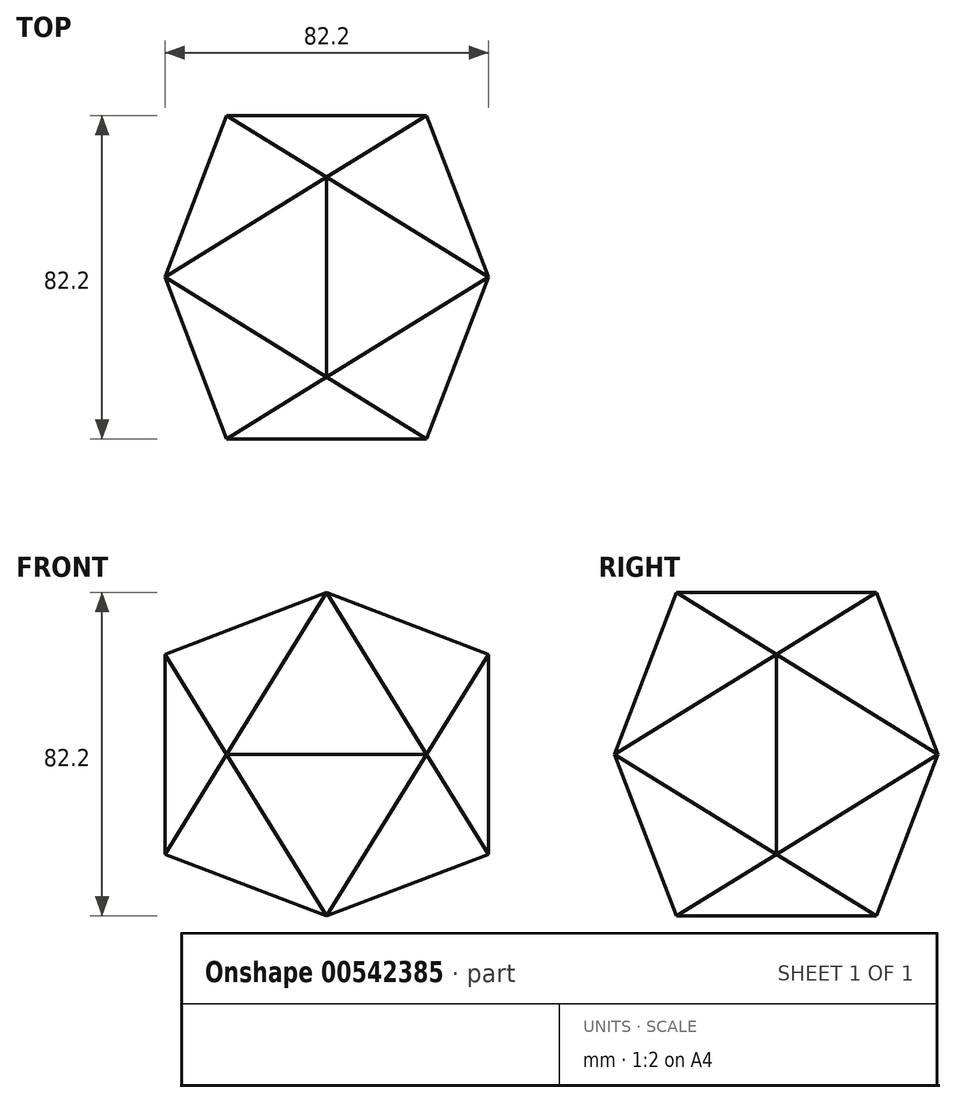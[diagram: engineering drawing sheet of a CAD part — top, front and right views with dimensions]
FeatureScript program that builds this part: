
annotation { "Feature Type Name" : "Feature", "Feature Type Description" : "" }
export const myFeature = defineFeature(function(context is Context, id is Id, definition is map)
    precondition{}
    {
        {
            var Q0;
            Q0=qCreatedBy(makeId("Front.planeOp"),FACE);
            var sketch = newSketch(context, id + "F0", { "sketchPlane" : qUnion([Q0])});
            skLineSegment(sketch, "E0.bottom", {"start": v(41.1, -25.4) * mm, "end": v(-41.1, -25.4) * mm});
            skLineSegment(sketch, "E0.top", {"start": v(41.1, 25.4) * mm, "end": v(-41.1, 25.4) * mm});
            skLineSegment(sketch, "E0.left", {"start": v(41.1, -25.4) * mm, "end": v(41.1, 25.4) * mm});
            skLineSegment(sketch, "E0.right", {"start": v(-41.1, -25.4) * mm, "end": v(-41.1, 25.4) * mm});
            skPoint(sketch, "E0.middle", {"position": v(0, 0) * mm});
            skSolve(sketch);
        }
        {
            var Q0;
            Q0=qCreatedBy(makeId("Front.planeOp"),FACE);
            var sketch = newSketch(context, id + "F1", { "sketchPlane" : qUnion([Q0])});
            skArc(sketch, "E1", {"start": v(0, -48.31) * mm, "mid": v(48.31, 0) * mm, "end": v(0, 48.31) * mm});
            skLineSegment(sketch, "E2", {"start": v(0, -48.31) * mm, "end": v(0, 48.31) * mm});
            skSolve(sketch);
        }
        {
            var Q0;
            Q0=makeQuery(id+"F1.imprint","IMPRINT",FACE,{"disambiguationData":[TD([[makeQuery(id+"F1.imprint","IMPRINT",EDGE,{"derivedFrom":sQuery(id+"F1.wireOp",EDGE,"E1")}),1.0]])]});
            var sketch = newSketch(context, id + "F2", { "sketchPlane" : qUnion([Q0])});
            skLineSegment(sketch, "E3", {"start": v(0, 0) * mm, "end": v(0, 112.6) * mm, "construction": true});
            skSolve(sketch);
        }
        {
            var Q0;
            Q0=makeQuery(id+"F1.imprint","IMPRINT",FACE,{"disambiguationData":[TD([[makeQuery(id+"F1.imprint","IMPRINT",EDGE,{"derivedFrom":sQuery(id+"F1.wireOp",EDGE,"E1")}),1.0]])]});
            var Q1;
            Q1=sQuery(id+"F1.wireOp",EDGE,"E1");
            var Q2;
            Q2=sQuery(id+"F2.wireOp",EDGE,"E3");
            revolve(context, id + "F3", {"entities" : qUnion([Q0]), "surfaceEntities" : qUnion([Q1]), "axis" : qUnion([Q2]), "revolveType" : RevolveType.FULL});
        }
        {
            var Q0;
            Q0=qCreatedBy(makeId("Top.planeOp"),FACE);
            var sketch = newSketch(context, id + "F4", { "sketchPlane" : qUnion([Q0])});
            skLineSegment(sketch, "E4.bottom", {"start": v(25.4, 41.1) * mm, "end": v(-25.4, 41.1) * mm});
            skLineSegment(sketch, "E4.top", {"start": v(25.4, -41.1) * mm, "end": v(-25.4, -41.1) * mm});
            skLineSegment(sketch, "E4.left", {"start": v(25.4, 41.1) * mm, "end": v(25.4, -41.1) * mm});
            skLineSegment(sketch, "E4.right", {"start": v(-25.4, 41.1) * mm, "end": v(-25.4, -41.1) * mm});
            skPoint(sketch, "E4.middle", {"position": v(0, 0) * mm});
            skSolve(sketch);
        }
        {
            var Q0;
            Q0=qCreatedBy(makeId("Right.planeOp"),FACE);
            var sketch = newSketch(context, id + "F5", { "sketchPlane" : qUnion([Q0])});
            skLineSegment(sketch, "E5.bottom", {"start": v(25.4, -41.1) * mm, "end": v(-25.4, -41.1) * mm});
            skLineSegment(sketch, "E5.top", {"start": v(25.4, 41.1) * mm, "end": v(-25.4, 41.1) * mm});
            skLineSegment(sketch, "E5.left", {"start": v(25.4, -41.1) * mm, "end": v(25.4, 41.1) * mm});
            skLineSegment(sketch, "E5.right", {"start": v(-25.4, -41.1) * mm, "end": v(-25.4, 41.1) * mm});
            skPoint(sketch, "E5.middle", {"position": v(0, 0) * mm});
            skSolve(sketch);
        }
        {
            var Q0;
            Q0=sQuery(id+"F5.wireOp",VERTEX,"E5.right.end");
            var Q1;
            Q1=sQuery(id+"F0.wireOp",VERTEX,"E0.left.end");
            var Q2;
            Q2=sQuery(id+"F5.wireOp",VERTEX,"E5.left.end");
            cPlane(context, id + "F6", {"entities" : qUnion([Q0, Q1, Q2]), "cplaneType" : CPlaneType.THREE_POINT, "offset" : 25.4 * mm, "width" : 152.4 * mm, "height" : 152.4 * mm});
        }
        {
            var Q0;
            Q0=qCreatedBy(id+"F6.planeOp",FACE);
            var sketch = newSketch(context, id + "F7", { "sketchPlane" : qUnion([Q0])});
            skCircle(sketch, "E6", {"center": v(0, 0) * mm, "radius": 29.33 * mm});
            skSolve(sketch);
        }
        {
            var Q0;
            Q0 = qSketchRegion(id + "F7", true);
            var Q1;
            Q1=makeQuery(id+"F3.opRevolve","SWEPT_BODY",BODY,{"disambiguationData":[OSD([sQuery(id+"F1.wireOp",EDGE,"E1")])]});
            extrude(context, id + "F8", {"entities" : qUnion([Q0]), "operationType" : NewBodyOperationType.REMOVE, "endBound" : BoundingType.UP_TO_NEXT, "oppositeDirection" : true, "depth" : 25.4 * mm, "endBoundEntityBody" : qUnion([Q1]), "offsetDistance" : 25.4 * mm});
        }
        {
            var Q0;
            Q0=sQuery(id+"F0.wireOp",VERTEX,"E0.right.end");
            var Q1;
            Q1=sQuery(id+"F5.wireOp",VERTEX,"E5.right.end");
            var Q2;
            Q2=sQuery(id+"F5.wireOp",VERTEX,"E5.left.end");
            cPlane(context, id + "F9", {"entities" : qUnion([Q0, Q1, Q2]), "cplaneType" : CPlaneType.THREE_POINT, "offset" : 25.4 * mm, "width" : 152.4 * mm, "height" : 152.4 * mm});
        }
        {
            var Q0;
            Q0=qCreatedBy(id+"F9.planeOp",FACE);
            var sketch = newSketch(context, id + "F10", { "sketchPlane" : qUnion([Q0])});
            skCircle(sketch, "E7", {"center": v(0, 0) * mm, "radius": 29.33 * mm});
            skSolve(sketch);
        }
        {
            var Q0;
            Q0 = qSketchRegion(id + "F10", true);
            extrude(context, id + "F11", {"entities" : qUnion([Q0]), "operationType" : NewBodyOperationType.REMOVE, "endBound" : BoundingType.UP_TO_NEXT, "oppositeDirection" : true, "depth" : 25.4 * mm, "offsetDistance" : 25.4 * mm});
        }
        {
            var Q0;
            Q0=sQuery(id+"F4.wireOp",VERTEX,"E4.right.end");
            var Q1;
            Q1=sQuery(id+"F0.wireOp",VERTEX,"E0.right.end");
            var Q2;
            Q2=sQuery(id+"F5.wireOp",VERTEX,"E5.right.end");
            cPlane(context, id + "F12", {"entities" : qUnion([Q0, Q1, Q2]), "cplaneType" : CPlaneType.THREE_POINT, "offset" : 25.4 * mm, "width" : 152.4 * mm, "height" : 152.4 * mm});
        }
        {
            var Q0;
            Q0=qCreatedBy(id+"F12.planeOp",FACE);
            var sketch = newSketch(context, id + "F13", { "sketchPlane" : qUnion([Q0])});
            skCircle(sketch, "E8", {"center": v(0, 0) * mm, "radius": 29.33 * mm});
            skSolve(sketch);
        }
        {
            var Q0;
            Q0 = qSketchRegion(id + "F13", true);
            extrude(context, id + "F14", {"entities" : qUnion([Q0]), "operationType" : NewBodyOperationType.REMOVE, "endBound" : BoundingType.UP_TO_NEXT, "depth" : 25.4 * mm, "offsetDistance" : 25.4 * mm});
        }
        {
            var Q0;
            Q0=sQuery(id+"F4.wireOp",VERTEX,"E4.right.end");
            var Q1;
            Q1=sQuery(id+"F5.wireOp",VERTEX,"E5.right.end");
            var Q2;
            Q2=sQuery(id+"F4.wireOp",VERTEX,"E4.left.end");
            cPlane(context, id + "F15", {"entities" : qUnion([Q0, Q1, Q2]), "cplaneType" : CPlaneType.THREE_POINT, "offset" : 25.4 * mm, "width" : 152.4 * mm, "height" : 152.4 * mm});
        }
        {
            var Q0;
            Q0=qCreatedBy(id+"F15.planeOp",FACE);
            var sketch = newSketch(context, id + "F16", { "sketchPlane" : qUnion([Q0])});
            skCircle(sketch, "E9", {"center": v(0, 0) * mm, "radius": 29.33 * mm});
            skSolve(sketch);
        }
        {
            var Q0;
            Q0 = qSketchRegion(id + "F16", true);
            extrude(context, id + "F17", {"entities" : qUnion([Q0]), "operationType" : NewBodyOperationType.REMOVE, "endBound" : BoundingType.UP_TO_NEXT, "depth" : 25.4 * mm, "offsetDistance" : 25.4 * mm});
        }
        {
            var Q0;
            Q0=sQuery(id+"F4.wireOp",VERTEX,"E4.left.end");
            var Q1;
            Q1=sQuery(id+"F5.wireOp",VERTEX,"E5.right.end");
            var Q2;
            Q2=sQuery(id+"F0.wireOp",VERTEX,"E0.left.end");
            cPlane(context, id + "F18", {"entities" : qUnion([Q0, Q1, Q2]), "cplaneType" : CPlaneType.THREE_POINT, "offset" : 25.4 * mm, "width" : 152.4 * mm, "height" : 152.4 * mm});
        }
        {
            var Q0;
            Q0=qCreatedBy(id+"F18.planeOp",FACE);
            var sketch = newSketch(context, id + "F19", { "sketchPlane" : qUnion([Q0])});
            skCircle(sketch, "E10", {"center": v(0, 0) * mm, "radius": 29.33 * mm});
            skSolve(sketch);
        }
        {
            var Q0;
            Q0 = qSketchRegion(id + "F19", true);
            extrude(context, id + "F20", {"entities" : qUnion([Q0]), "operationType" : NewBodyOperationType.REMOVE, "endBound" : BoundingType.UP_TO_NEXT, "depth" : 25.4 * mm, "offsetDistance" : 25.4 * mm});
        }
        {
            var Q0;
            Q0=sQuery(id+"F4.wireOp",VERTEX,"E4.left.start");
            var Q1;
            Q1=sQuery(id+"F0.wireOp",VERTEX,"E0.left.end");
            var Q2;
            Q2=sQuery(id+"F5.wireOp",VERTEX,"E5.left.end");
            cPlane(context, id + "F21", {"entities" : qUnion([Q0, Q1, Q2]), "cplaneType" : CPlaneType.THREE_POINT, "offset" : 25.4 * mm, "width" : 152.4 * mm, "height" : 152.4 * mm});
        }
        {
            var Q0;
            Q0=qCreatedBy(id+"F21.planeOp",FACE);
            var sketch = newSketch(context, id + "F22", { "sketchPlane" : qUnion([Q0])});
            skCircle(sketch, "E11", {"center": v(0, 0) * mm, "radius": 29.33 * mm});
            skSolve(sketch);
        }
        {
            var Q0;
            Q0 = qSketchRegion(id + "F22", true);
            extrude(context, id + "F23", {"entities" : qUnion([Q0]), "operationType" : NewBodyOperationType.REMOVE, "endBound" : BoundingType.UP_TO_NEXT, "depth" : 25.4 * mm, "offsetDistance" : 25.4 * mm});
        }
        {
            var Q0;
            Q0=sQuery(id+"F4.wireOp",VERTEX,"E4.left.start");
            var Q1;
            Q1=sQuery(id+"F4.wireOp",VERTEX,"E4.right.start");
            var Q2;
            Q2=sQuery(id+"F5.wireOp",VERTEX,"E5.left.end");
            cPlane(context, id + "F24", {"entities" : qUnion([Q0, Q1, Q2]), "cplaneType" : CPlaneType.THREE_POINT, "offset" : 25.4 * mm, "width" : 152.4 * mm, "height" : 152.4 * mm});
        }
        {
            var Q0;
            Q0=qCreatedBy(id+"F24.planeOp",FACE);
            var sketch = newSketch(context, id + "F25", { "sketchPlane" : qUnion([Q0])});
            skCircle(sketch, "E12", {"center": v(0, 0) * mm, "radius": 29.33 * mm});
            skSolve(sketch);
        }
        {
            var Q0;
            Q0 = qSketchRegion(id + "F25", true);
            extrude(context, id + "F26", {"entities" : qUnion([Q0]), "operationType" : NewBodyOperationType.REMOVE, "endBound" : BoundingType.UP_TO_NEXT, "oppositeDirection" : true, "depth" : 25.4 * mm, "offsetDistance" : 25.4 * mm});
        }
        {
            var Q0;
            Q0=sQuery(id+"F4.wireOp",VERTEX,"E4.right.start");
            var Q1;
            Q1=sQuery(id+"F5.wireOp",VERTEX,"E5.left.end");
            var Q2;
            Q2=sQuery(id+"F0.wireOp",VERTEX,"E0.right.end");
            cPlane(context, id + "F27", {"entities" : qUnion([Q0, Q1, Q2]), "cplaneType" : CPlaneType.THREE_POINT, "offset" : 25.4 * mm, "width" : 152.4 * mm, "height" : 152.4 * mm});
        }
        {
            var Q0;
            Q0=qCreatedBy(id+"F27.planeOp",FACE);
            var sketch = newSketch(context, id + "F28", { "sketchPlane" : qUnion([Q0])});
            skCircle(sketch, "E13", {"center": v(0, 0) * mm, "radius": 29.33 * mm});
            skSolve(sketch);
        }
        {
            var Q0;
            Q0 = qSketchRegion(id + "F28", true);
            extrude(context, id + "F29", {"entities" : qUnion([Q0]), "operationType" : NewBodyOperationType.REMOVE, "endBound" : BoundingType.UP_TO_NEXT, "depth" : 25.4 * mm, "offsetDistance" : 25.4 * mm});
        }
        {
            var Q0;
            Q0=sQuery(id+"F0.wireOp",VERTEX,"E0.left.end");
            var Q1;
            Q1=sQuery(id+"F4.wireOp",VERTEX,"E4.left.end");
            var Q2;
            Q2=sQuery(id+"F0.wireOp",VERTEX,"E0.bottom.start");
            cPlane(context, id + "F30", {"entities" : qUnion([Q0, Q1, Q2]), "cplaneType" : CPlaneType.THREE_POINT, "offset" : 25.4 * mm, "width" : 152.4 * mm, "height" : 152.4 * mm});
        }
        {
            var Q0;
            Q0=qCreatedBy(id+"F30.planeOp",FACE);
            var sketch = newSketch(context, id + "F31", { "sketchPlane" : qUnion([Q0])});
            skCircle(sketch, "E14", {"center": v(0, 0) * mm, "radius": 29.33 * mm});
            skSolve(sketch);
        }
        {
            var Q0;
            Q0 = qSketchRegion(id + "F31", true);
            extrude(context, id + "F32", {"entities" : qUnion([Q0]), "operationType" : NewBodyOperationType.REMOVE, "endBound" : BoundingType.UP_TO_NEXT, "oppositeDirection" : true, "depth" : 25.4 * mm, "offsetDistance" : 25.4 * mm});
        }
        {
            var Q0;
            Q0=sQuery(id+"F0.wireOp",VERTEX,"E0.bottom.start");
            var Q1;
            Q1=sQuery(id+"F4.wireOp",VERTEX,"E4.left.start");
            var Q2;
            Q2=sQuery(id+"F0.wireOp",VERTEX,"E0.left.end");
            cPlane(context, id + "F33", {"entities" : qUnion([Q0, Q1, Q2]), "cplaneType" : CPlaneType.THREE_POINT, "offset" : 25.4 * mm, "width" : 152.4 * mm, "height" : 152.4 * mm});
        }
        {
            var Q0;
            Q0=qCreatedBy(id+"F33.planeOp",FACE);
            var sketch = newSketch(context, id + "F34", { "sketchPlane" : qUnion([Q0])});
            skCircle(sketch, "E15", {"center": v(0, 0) * mm, "radius": 29.33 * mm});
            skSolve(sketch);
        }
        {
            var Q0;
            Q0 = qSketchRegion(id + "F34", true);
            extrude(context, id + "F35", {"entities" : qUnion([Q0]), "operationType" : NewBodyOperationType.REMOVE, "endBound" : BoundingType.UP_TO_NEXT, "oppositeDirection" : true, "depth" : 25.4 * mm, "offsetDistance" : 25.4 * mm});
        }
        {
            var Q0;
            Q0=sQuery(id+"F0.wireOp",VERTEX,"E0.right.end");
            var Q1;
            Q1=sQuery(id+"F0.wireOp",VERTEX,"E0.right.start");
            var Q2;
            Q2=sQuery(id+"F4.wireOp",VERTEX,"E4.right.end");
            cPlane(context, id + "F36", {"entities" : qUnion([Q0, Q1, Q2]), "cplaneType" : CPlaneType.THREE_POINT, "offset" : 25.4 * mm, "width" : 152.4 * mm, "height" : 152.4 * mm});
        }
        {
            var Q0;
            Q0=qCreatedBy(id+"F36.planeOp",FACE);
            var sketch = newSketch(context, id + "F37", { "sketchPlane" : qUnion([Q0])});
            skCircle(sketch, "E16", {"center": v(0, 0) * mm, "radius": 29.33 * mm});
            skSolve(sketch);
        }
        {
            var Q0;
            Q0 = qSketchRegion(id + "F37", true);
            extrude(context, id + "F38", {"entities" : qUnion([Q0]), "operationType" : NewBodyOperationType.REMOVE, "endBound" : BoundingType.UP_TO_NEXT, "oppositeDirection" : true, "depth" : 25.4 * mm, "offsetDistance" : 25.4 * mm});
        }
        {
            var Q0;
            Q0=sQuery(id+"F0.wireOp",VERTEX,"E0.right.end");
            var Q1;
            Q1=sQuery(id+"F4.wireOp",VERTEX,"E4.right.start");
            var Q2;
            Q2=sQuery(id+"F0.wireOp",VERTEX,"E0.right.start");
            cPlane(context, id + "F39", {"entities" : qUnion([Q0, Q1, Q2]), "cplaneType" : CPlaneType.THREE_POINT, "offset" : 25.4 * mm, "width" : 152.4 * mm, "height" : 152.4 * mm});
        }
        {
            var Q0;
            Q0=qCreatedBy(id+"F39.planeOp",FACE);
            var sketch = newSketch(context, id + "F40", { "sketchPlane" : qUnion([Q0])});
            skCircle(sketch, "E17", {"center": v(0, 0) * mm, "radius": 29.33 * mm});
            skSolve(sketch);
        }
        {
            var Q0;
            Q0 = qSketchRegion(id + "F40", true);
            extrude(context, id + "F41", {"entities" : qUnion([Q0]), "operationType" : NewBodyOperationType.REMOVE, "endBound" : BoundingType.UP_TO_NEXT, "oppositeDirection" : true, "depth" : 25.4 * mm, "offsetDistance" : 25.4 * mm});
        }
        {
            var Q0;
            Q0=sQuery(id+"F4.wireOp",VERTEX,"E4.right.start");
            var Q1;
            Q1=sQuery(id+"F5.wireOp",VERTEX,"E5.left.start");
            var Q2;
            Q2=sQuery(id+"F0.wireOp",VERTEX,"E0.right.start");
            cPlane(context, id + "F42", {"entities" : qUnion([Q0, Q1, Q2]), "cplaneType" : CPlaneType.THREE_POINT, "offset" : 25.4 * mm, "width" : 152.4 * mm, "height" : 152.4 * mm});
        }
        {
            var Q0;
            Q0=qCreatedBy(id+"F42.planeOp",FACE);
            var sketch = newSketch(context, id + "F43", { "sketchPlane" : qUnion([Q0])});
            skCircle(sketch, "E18", {"center": v(0, 0) * mm, "radius": 29.33 * mm});
            skSolve(sketch);
        }
        {
            var Q0;
            Q0 = qSketchRegion(id + "F43", true);
            extrude(context, id + "F44", {"entities" : qUnion([Q0]), "operationType" : NewBodyOperationType.REMOVE, "endBound" : BoundingType.UP_TO_NEXT, "oppositeDirection" : true, "depth" : 25.4 * mm, "offsetDistance" : 25.4 * mm});
        }
        {
            var Q0;
            Q0=sQuery(id+"F5.wireOp",VERTEX,"E5.left.start");
            var Q1;
            Q1=sQuery(id+"F4.wireOp",VERTEX,"E4.right.start");
            var Q2;
            Q2=sQuery(id+"F4.wireOp",VERTEX,"E4.left.start");
            cPlane(context, id + "F45", {"entities" : qUnion([Q0, Q1, Q2]), "cplaneType" : CPlaneType.THREE_POINT, "offset" : 25.4 * mm, "width" : 152.4 * mm, "height" : 152.4 * mm});
        }
        {
            var Q0;
            Q0=qCreatedBy(id+"F45.planeOp",FACE);
            var sketch = newSketch(context, id + "F46", { "sketchPlane" : qUnion([Q0])});
            skCircle(sketch, "E19", {"center": v(0, 0) * mm, "radius": 29.33 * mm});
            skSolve(sketch);
        }
        {
            var Q0;
            Q0 = qSketchRegion(id + "F46", true);
            extrude(context, id + "F47", {"entities" : qUnion([Q0]), "operationType" : NewBodyOperationType.REMOVE, "endBound" : BoundingType.UP_TO_NEXT, "oppositeDirection" : true, "depth" : 25.4 * mm, "offsetDistance" : 25.4 * mm});
        }
        {
            var Q0;
            Q0=sQuery(id+"F4.wireOp",VERTEX,"E4.left.start");
            var Q1;
            Q1=sQuery(id+"F0.wireOp",VERTEX,"E0.bottom.start");
            var Q2;
            Q2=sQuery(id+"F5.wireOp",VERTEX,"E5.left.start");
            cPlane(context, id + "F48", {"entities" : qUnion([Q0, Q1, Q2]), "cplaneType" : CPlaneType.THREE_POINT, "offset" : 25.4 * mm, "width" : 152.4 * mm, "height" : 152.4 * mm});
        }
        {
            var Q0;
            Q0=qCreatedBy(id+"F48.planeOp",FACE);
            var sketch = newSketch(context, id + "F49", { "sketchPlane" : qUnion([Q0])});
            skCircle(sketch, "E20", {"center": v(0, 0) * mm, "radius": 29.33 * mm});
            skSolve(sketch);
        }
        {
            var Q0;
            Q0 = qSketchRegion(id + "F49", true);
            extrude(context, id + "F50", {"entities" : qUnion([Q0]), "operationType" : NewBodyOperationType.REMOVE, "endBound" : BoundingType.UP_TO_NEXT, "oppositeDirection" : true, "depth" : 25.4 * mm, "offsetDistance" : 25.4 * mm});
        }
        {
            var Q0;
            Q0=sQuery(id+"F4.wireOp",VERTEX,"E4.left.end");
            var Q1;
            Q1=sQuery(id+"F5.wireOp",VERTEX,"E5.right.start");
            var Q2;
            Q2=sQuery(id+"F0.wireOp",VERTEX,"E0.bottom.start");
            cPlane(context, id + "F51", {"entities" : qUnion([Q0, Q1, Q2]), "cplaneType" : CPlaneType.THREE_POINT, "offset" : 25.4 * mm, "width" : 152.4 * mm, "height" : 152.4 * mm});
        }
        {
            var Q0;
            Q0=qCreatedBy(id+"F51.planeOp",FACE);
            var sketch = newSketch(context, id + "F52", { "sketchPlane" : qUnion([Q0])});
            skCircle(sketch, "E21", {"center": v(0, 0) * mm, "radius": 29.33 * mm});
            skSolve(sketch);
        }
        {
            var Q0;
            Q0 = qSketchRegion(id + "F52", true);
            extrude(context, id + "F53", {"entities" : qUnion([Q0]), "operationType" : NewBodyOperationType.REMOVE, "endBound" : BoundingType.UP_TO_NEXT, "oppositeDirection" : true, "depth" : 25.4 * mm, "offsetDistance" : 25.4 * mm});
        }
        {
            var Q0;
            Q0=sQuery(id+"F5.wireOp",VERTEX,"E5.left.start");
            var Q1;
            Q1=sQuery(id+"F0.wireOp",VERTEX,"E0.bottom.start");
            var Q2;
            Q2=sQuery(id+"F5.wireOp",VERTEX,"E5.right.start");
            cPlane(context, id + "F54", {"entities" : qUnion([Q0, Q1, Q2]), "cplaneType" : CPlaneType.THREE_POINT, "offset" : 25.4 * mm, "width" : 152.4 * mm, "height" : 152.4 * mm});
        }
        {
            var Q0;
            Q0=qCreatedBy(id+"F54.planeOp",FACE);
            var sketch = newSketch(context, id + "F55", { "sketchPlane" : qUnion([Q0])});
            skCircle(sketch, "E22", {"center": v(0, 0) * mm, "radius": 29.33 * mm});
            skSolve(sketch);
        }
        {
            var Q0;
            Q0 = qSketchRegion(id + "F55", true);
            extrude(context, id + "F56", {"entities" : qUnion([Q0]), "operationType" : NewBodyOperationType.REMOVE, "endBound" : BoundingType.UP_TO_NEXT, "oppositeDirection" : true, "depth" : 25.4 * mm, "offsetDistance" : 25.4 * mm});
        }
        {
            var Q0;
            Q0=sQuery(id+"F5.wireOp",VERTEX,"E5.right.start");
            var Q1;
            Q1=sQuery(id+"F4.wireOp",VERTEX,"E4.left.end");
            var Q2;
            Q2=sQuery(id+"F4.wireOp",VERTEX,"E4.right.end");
            cPlane(context, id + "F57", {"entities" : qUnion([Q0, Q1, Q2]), "cplaneType" : CPlaneType.THREE_POINT, "offset" : 25.4 * mm, "width" : 152.4 * mm, "height" : 152.4 * mm});
        }
        {
            var Q0;
            Q0=qCreatedBy(id+"F57.planeOp",FACE);
            var sketch = newSketch(context, id + "F58", { "sketchPlane" : qUnion([Q0])});
            skCircle(sketch, "E23", {"center": v(0, 0) * mm, "radius": 29.33 * mm});
            skSolve(sketch);
        }
        {
            var Q0;
            Q0 = qSketchRegion(id + "F58", true);
            extrude(context, id + "F59", {"entities" : qUnion([Q0]), "operationType" : NewBodyOperationType.REMOVE, "endBound" : BoundingType.UP_TO_NEXT, "oppositeDirection" : true, "depth" : 25.4 * mm, "offsetDistance" : 25.4 * mm});
        }
        {
            var Q0;
            Q0=sQuery(id+"F5.wireOp",VERTEX,"E5.left.start");
            var Q1;
            Q1=sQuery(id+"F5.wireOp",VERTEX,"E5.right.start");
            var Q2;
            Q2=sQuery(id+"F0.wireOp",VERTEX,"E0.right.start");
            cPlane(context, id + "F60", {"entities" : qUnion([Q0, Q1, Q2]), "cplaneType" : CPlaneType.THREE_POINT, "offset" : 25.4 * mm, "width" : 152.4 * mm, "height" : 152.4 * mm});
        }
        {
            var Q0;
            Q0=qCreatedBy(id+"F60.planeOp",FACE);
            var sketch = newSketch(context, id + "F61", { "sketchPlane" : qUnion([Q0])});
            skCircle(sketch, "E24", {"center": v(0, 0) * mm, "radius": 29.33 * mm});
            skSolve(sketch);
        }
        {
            var Q0;
            Q0=sQuery(id+"F0.wireOp",VERTEX,"E0.right.start");
            var Q1;
            Q1=sQuery(id+"F4.wireOp",VERTEX,"E4.right.end");
            var Q2;
            Q2=sQuery(id+"F5.wireOp",VERTEX,"E5.right.start");
            cPlane(context, id + "F62", {"entities" : qUnion([Q0, Q1, Q2]), "cplaneType" : CPlaneType.THREE_POINT, "offset" : 25.4 * mm, "width" : 152.4 * mm, "height" : 152.4 * mm});
        }
        {
            var Q0;
            Q0=qCreatedBy(id+"F62.planeOp",FACE);
            var sketch = newSketch(context, id + "F63", { "sketchPlane" : qUnion([Q0])});
            skCircle(sketch, "E25", {"center": v(0, 0) * mm, "radius": 29.33 * mm});
            skSolve(sketch);
        }
        {
            var Q0;
            Q0 = qSketchRegion(id + "F61", true);
            extrude(context, id + "F64", {"entities" : qUnion([Q0]), "operationType" : NewBodyOperationType.REMOVE, "endBound" : BoundingType.UP_TO_NEXT, "oppositeDirection" : true, "depth" : 25.4 * mm, "offsetDistance" : 25.4 * mm});
        }
        {
            var Q0;
            Q0 = qSketchRegion(id + "F63", true);
            extrude(context, id + "F65", {"entities" : qUnion([Q0]), "operationType" : NewBodyOperationType.REMOVE, "endBound" : BoundingType.UP_TO_NEXT, "depth" : 25.4 * mm, "offsetDistance" : 25.4 * mm});
        }
    });
